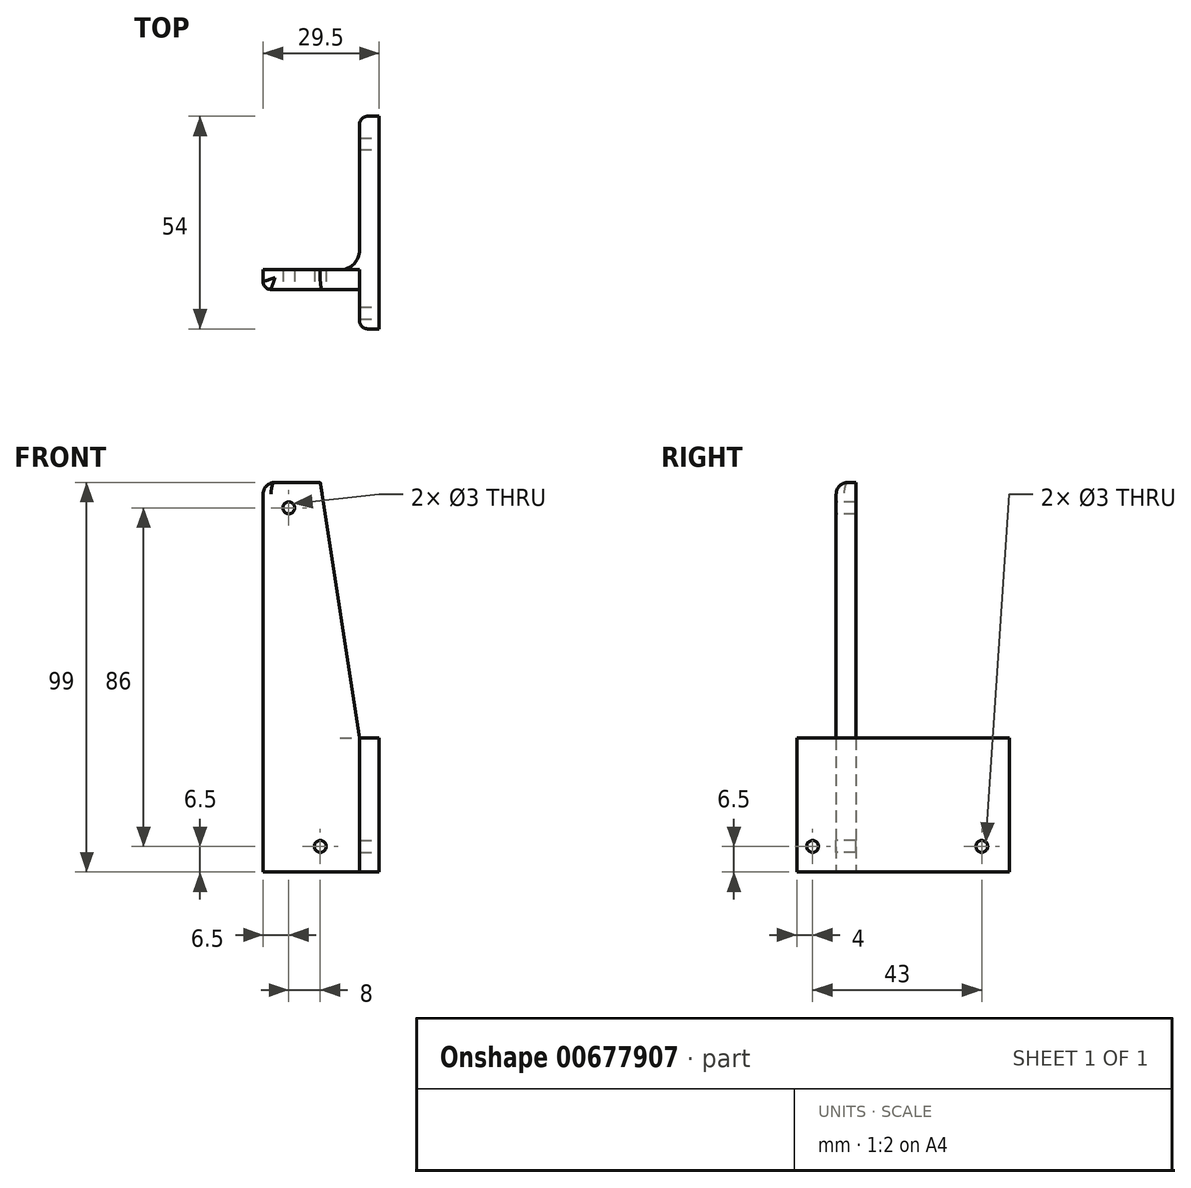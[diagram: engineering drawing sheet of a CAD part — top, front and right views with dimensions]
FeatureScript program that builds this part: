
annotation { "Feature Type Name" : "Feature", "Feature Type Description" : "" }
export const myFeature = defineFeature(function(context is Context, id is Id, definition is map)
    precondition{}
    {
        {
            var Q0;
            Q0=qCreatedBy(makeId("Top.planeOp"),FACE);
            var sketch = newSketch(context, id + "F0", { "sketchPlane" : qUnion([Q0])});
            skLineSegment(sketch, "E0", {"start": v(0, 0) * mm, "end": v(0, 54) * mm});
            skLineSegment(sketch, "E1", {"start": v(0, 54) * mm, "end": v(-5, 54) * mm});
            skLineSegment(sketch, "E2", {"start": v(-5, 54) * mm, "end": v(-5, 15) * mm});
            skLineSegment(sketch, "E3", {"start": v(-5, 15) * mm, "end": v(-29.5, 15) * mm});
            skLineSegment(sketch, "E4", {"start": v(-29.5, 15) * mm, "end": v(-29.5, 10) * mm});
            skLineSegment(sketch, "E5", {"start": v(-29.5, 10) * mm, "end": v(-5, 10) * mm});
            skLineSegment(sketch, "E6", {"start": v(-5, 10) * mm, "end": v(-5, 0) * mm});
            skLineSegment(sketch, "E7", {"start": v(-5, 0) * mm, "end": v(0, 0) * mm});
            skSolve(sketch);
        }
        {
            var Q0;
            Q0=makeQuery(id+"F0.imprint","IMPRINT",FACE,{"disambiguationData":[TD([[makeQuery(id+"F0.imprint","IMPRINT",EDGE,{"derivedFrom":sQuery(id+"F0.wireOp",EDGE,"E0")}),1.0]])]});
            extrude(context, id + "F1", {"entities" : qUnion([Q0]), "depth" : (86 + 6.5 + 6.5) * mm, "offsetDistance" : 25 * mm});
        }
        {
            var Q0;
            Q0=makeQuery(id+"F1.opExtrude","SWEPT_FACE",FACE,{"disambiguationData":[OSD([sQuery(id+"F0.wireOp",EDGE,"E5")])]});
            var sketch = newSketch(context, id + "F2", { "sketchPlane" : qUnion([Q0])});
            skLineSegment(sketch, "E8", {"start": v(-29.5, 99) * mm, "end": v(-15, 99) * mm});
            skLineSegment(sketch, "E9", {"start": v(-15, 99) * mm, "end": v(-5, 34) * mm});
            skLineSegment(sketch, "E10", {"start": v(-5, 34) * mm, "end": v(0, 34) * mm});
            skLineSegment(sketch, "E11", {"start": v(0, 34) * mm, "end": v(0, 108.76) * mm});
            skLineSegment(sketch, "E12", {"start": v(0, 108.76) * mm, "end": v(-29.5, 108.76) * mm});
            skLineSegment(sketch, "E13", {"start": v(-29.5, 108.76) * mm, "end": v(-29.5, 99) * mm});
            skSolve(sketch);
        }
        {
            var Q0;
            {var subQ0=sQuery(id+"F2.wireOp",EDGE,"E9");Q0=makeQuery(id+"F2.imprint","IMPRINT",FACE,{"disambiguationData":[TD([[makeQuery(id+"F2.imprint","IMPRINT",EDGE,{"derivedFrom":subQ0}),1.0]])]});}
            var Q1;
            {var subQ1=sQuery(id+"F2.wireOp",EDGE,"E8");Q1=makeQuery(id+"F2.imprint","IMPRINT",FACE,{"disambiguationData":[TD([[makeQuery(id+"F2.imprint","IMPRINT",EDGE,{"derivedFrom":subQ1}),1.0]])]});}
            extrude(context, id + "F3", {"entities" : qUnion([Q0, Q1]), "operationType" : NewBodyOperationType.REMOVE, "endBound" : BoundingType.SYMMETRIC, "oppositeDirection" : true, "depth" : 100 * mm, "offsetDistance" : 25 * mm});
        }
        {
            var Q0;
            Q0=makeQuery(id+"F1.opExtrude","SWEPT_FACE",FACE,{"disambiguationData":[OSD([sQuery(id+"F0.wireOp",EDGE,"E0")])]});
            var sketch = newSketch(context, id + "F4", { "sketchPlane" : qUnion([Q0])});
            skCircle(sketch, "E14", {"center": v(4, 6.5) * mm, "radius": 1.5 * mm});
            skCircle(sketch, "E15", {"center": v(47, 6.5) * mm, "radius": 1.5 * mm});
            skSolve(sketch);
        }
        {
            var Q0;
            Q0 = qSketchRegion(id + "F4", true);
            extrude(context, id + "F5", {"entities" : qUnion([Q0]), "operationType" : NewBodyOperationType.REMOVE, "oppositeDirection" : true, "depth" : 25 * mm, "offsetDistance" : 25 * mm});
        }
        {
            var Q0;
            Q0=makeQuery(id+"F1.opExtrude","SWEPT_FACE",FACE,{"disambiguationData":[OSD([sQuery(id+"F0.wireOp",EDGE,"E5")])]});
            var sketch = newSketch(context, id + "F6", { "sketchPlane" : qUnion([Q0])});
            skCircle(sketch, "E16", {"center": v(-15, 6.5) * mm, "radius": 1.5 * mm});
            skCircle(sketch, "E17", {"center": v(-23, 92.5) * mm, "radius": 1.5 * mm});
            skSolve(sketch);
        }
        {
            var Q0;
            Q0=makeQuery(id+"F6.imprint","IMPRINT",FACE,{"disambiguationData":[TD([[makeQuery(id+"F6.imprint","IMPRINT",EDGE,{"derivedFrom":sQuery(id+"F6.wireOp",EDGE,"E17")}),1.0]])]});
            var Q1;
            Q1=makeQuery(id+"F6.imprint","IMPRINT",FACE,{"disambiguationData":[TD([[makeQuery(id+"F6.imprint","IMPRINT",EDGE,{"derivedFrom":sQuery(id+"F6.wireOp",EDGE,"E16")}),1.0]])]});
            extrude(context, id + "F7", {"entities" : qUnion([Q0, Q1]), "operationType" : NewBodyOperationType.REMOVE, "oppositeDirection" : true, "depth" : 25 * mm, "offsetDistance" : 25 * mm});
        }
        {
            var Q0;
            Q0=makeQuery(id+"F1.opExtrude","SWEPT_EDGE",EDGE,{"disambiguationData":[OSD([sQuery(id+"F0.wireOp",EDGE,"E2"),sQuery(id+"F0.wireOp",EDGE,"E3")])]});
            fillet(context, id + "F8", {"entities" : qUnion([Q0]), "radius" : 5 * mm, "tangentPropagation" : true, "allowEdgeOverflow" : false});
        }
        {
            var Q0;
            Q0=makeQuery(id+"F1.opExtrude","SWEPT_FACE",FACE,{"disambiguationData":[OSD([sQuery(id+"F0.wireOp",EDGE,"E0")])]});
            var sketch = newSketch(context, id + "F9", { "sketchPlane" : qUnion([Q0])});
            skLineSegment(sketch, "E18", {"start": v(54, 34) * mm, "end": v(15, 34) * mm});
            skLineSegment(sketch, "E19", {"start": v(15, 34) * mm, "end": v(15, 114) * mm});
            skLineSegment(sketch, "E20", {"start": v(15, 114) * mm, "end": v(54, 114) * mm});
            skLineSegment(sketch, "E21", {"start": v(54, 114) * mm, "end": v(54, 34) * mm});
            skSolve(sketch);
        }
        {
            var Q0;
            Q0=makeQuery(id+"F9.imprint","IMPRINT",FACE,{"disambiguationData":[TD([[makeQuery(id+"F9.imprint","IMPRINT",EDGE,{"derivedFrom":sQuery(id+"F9.wireOp",EDGE,"E18")}),-1.0]])]});
            extrude(context, id + "F10", {"entities" : qUnion([Q0]), "operationType" : NewBodyOperationType.REMOVE, "oppositeDirection" : true, "depth" : 25 * mm, "offsetDistance" : 25 * mm});
        }
        {
            var Q0;
            Q0=makeQuery(id+"F1.opExtrude","SWEPT_EDGE",EDGE,{"disambiguationData":[OSD([sQuery(id+"F0.wireOp",EDGE,"E1"),sQuery(id+"F0.wireOp",EDGE,"E2")])]});
            var Q1;
            Q1=makeQuery(id+"F1.opExtrude","SWEPT_EDGE",EDGE,{"disambiguationData":[OSD([sQuery(id+"F0.wireOp",EDGE,"E6"),sQuery(id+"F0.wireOp",EDGE,"E7")])]});
            var Q2;
            Q2=makeQuery(id+"F1.opExtrude","SWEPT_EDGE",EDGE,{"disambiguationData":[OSD([sQuery(id+"F0.wireOp",EDGE,"E4"),sQuery(id+"F0.wireOp",EDGE,"E5")])]});
            fillet(context, id + "F11", {"entities" : qUnion([Q0, Q1, Q2]), "radius" : 2 * mm, "tangentPropagation" : true, "allowEdgeOverflow" : false});
        }
        {
            var Q0;
            Q0=makeQuery(id+"F3.boolean.opBoolean","COPY",EDGE,{"derivedFrom":makeQuery(id+"F3.opExtrude","SWEPT_EDGE",EDGE,{"disambiguationData":[OSD([sQuery(id+"F0.wireOp",EDGE,"E5"),sQuery(id+"F2.wireOp",EDGE,"E8"),sQuery(id+"F2.wireOp",EDGE,"E9")])]})});
            var Q1;
            Q1=makeQuery(id+"F1.opExtrude","CAP_EDGE",EDGE,{"disambiguationData":[OSD([sQuery(id+"F0.wireOp",EDGE,"E4")])],"isStart":false});
            fillet(context, id + "F12", {"entities" : qUnion([Q0, Q1]), "radius" : 3 * mm, "tangentPropagation" : true, "allowEdgeOverflow" : false});
        }
    });
